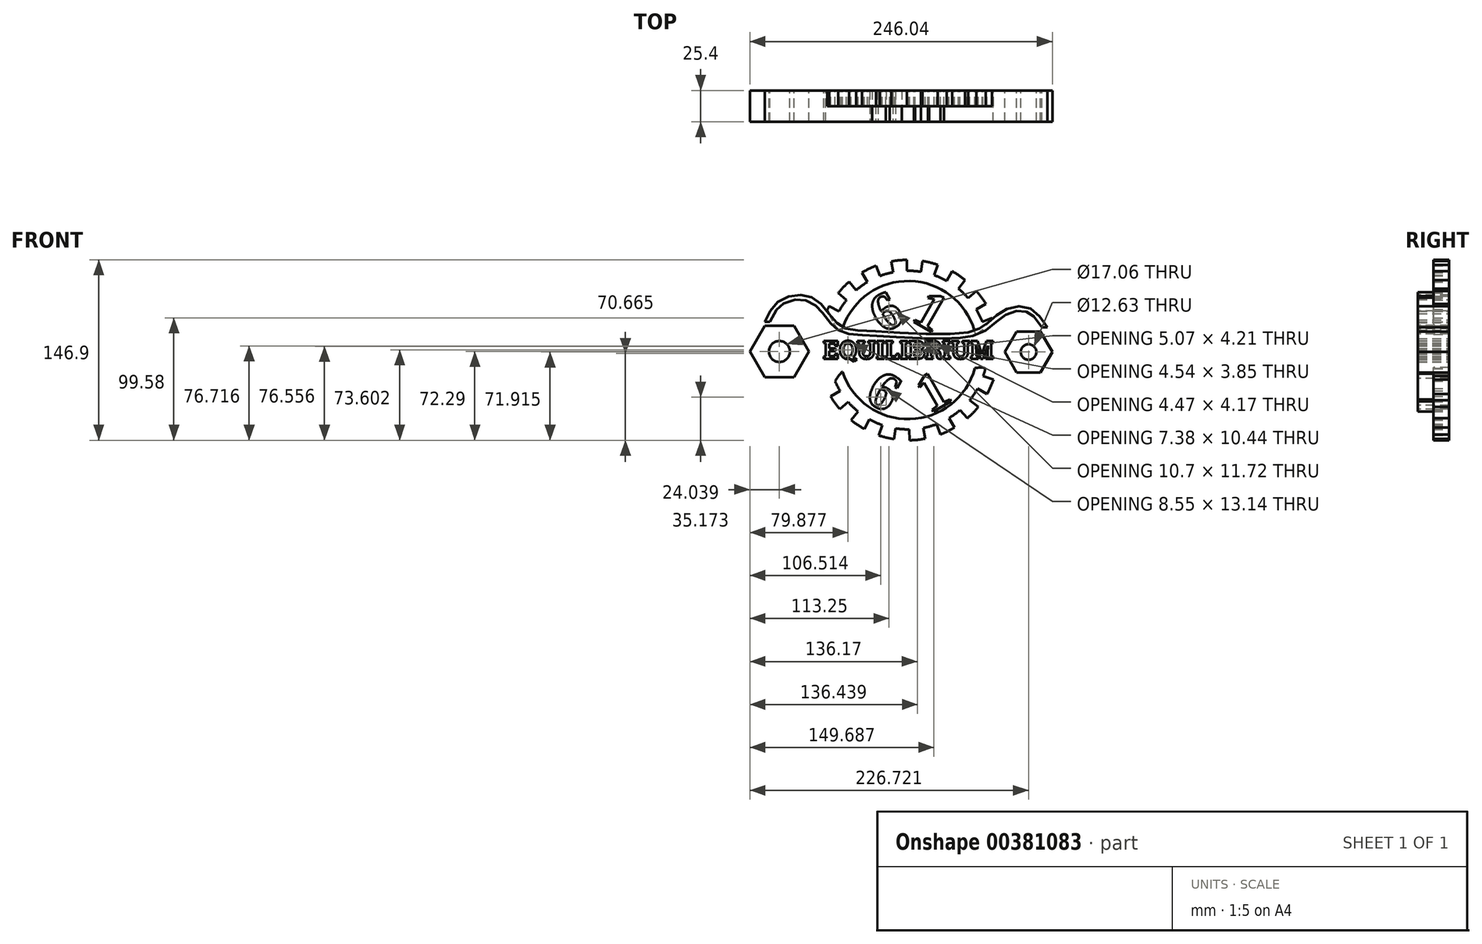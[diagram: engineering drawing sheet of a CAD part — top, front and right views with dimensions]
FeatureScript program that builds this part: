
annotation { "Feature Type Name" : "Feature", "Feature Type Description" : "" }
export const myFeature = defineFeature(function(context is Context, id is Id, definition is map)
    precondition{}
    {
        {
            var Q0;
            Q0=qCreatedBy(makeId("Front.planeOp"),FACE);
            var sketch = newSketch(context, id + "F0", { "sketchPlane" : qUnion([Q0])});
            skCircle(sketch, "E0.cCircle", {"center": v(93.86, 118.06) * mm, "radius": 16.73 * mm, "construction": true});
            skLineSegment(sketch, "E0.0", {"start": v(74.54, 118.06) * mm, "end": v(84.2, 134.79) * mm});
            skLineSegment(sketch, "E0.1", {"start": v(84.2, 134.79) * mm, "end": v(103.52, 134.79) * mm});
            skLineSegment(sketch, "E0.2", {"start": v(103.52, 134.79) * mm, "end": v(113.18, 118.06) * mm});
            skLineSegment(sketch, "E0.3", {"start": v(113.18, 118.06) * mm, "end": v(103.52, 101.32) * mm});
            skLineSegment(sketch, "E0.4", {"start": v(103.52, 101.32) * mm, "end": v(84.2, 101.32) * mm});
            skLineSegment(sketch, "E0.5", {"start": v(84.2, 101.32) * mm, "end": v(74.54, 118.06) * mm});
            skPoint(sketch, "E0.0.midPoint", {"position": v(79.37, 126.42) * mm});
            skCircle(sketch, "E1.cCircle", {"center": v(-108.82, 118.43) * mm, "radius": 20.82 * mm, "construction": true});
            skLineSegment(sketch, "E1.0", {"start": v(-84.78, 118.43) * mm, "end": v(-96.8, 97.61) * mm});
            skLineSegment(sketch, "E1.1", {"start": v(-96.8, 97.61) * mm, "end": v(-120.84, 97.61) * mm});
            skLineSegment(sketch, "E1.2", {"start": v(-120.84, 97.61) * mm, "end": v(-132.86, 118.43) * mm});
            skLineSegment(sketch, "E1.3", {"start": v(-132.86, 118.43) * mm, "end": v(-120.84, 139.25) * mm});
            skLineSegment(sketch, "E1.4", {"start": v(-120.84, 139.25) * mm, "end": v(-96.8, 139.25) * mm});
            skLineSegment(sketch, "E1.5", {"start": v(-96.8, 139.25) * mm, "end": v(-84.78, 118.43) * mm});
            skPoint(sketch, "E1.0.midPoint", {"position": v(-90.8, 108.02) * mm});
            skCircle(sketch, "E2", {"center": v(-108.82, 118.43) * mm, "radius": 8.53 * mm});
            skCircle(sketch, "E3", {"center": v(93.86, 118.06) * mm, "radius": 6.32 * mm});
            skLineSegment(sketch, "E4.0", {"start": v(82.3, 138.1) * mm, "end": v(109.3, 138.1) * mm});
            skLineSegment(sketch, "E4.1", {"start": v(70.73, 118.06) * mm, "end": v(82.3, 138.1) * mm});
            skLineSegment(sketch, "E4.2", {"start": v(82.3, 98.02) * mm, "end": v(70.73, 118.06) * mm});
            skLineSegment(sketch, "E4.3", {"start": v(103.52, 98.02) * mm, "end": v(82.3, 98.02) * mm});
            skLineSegment(sketch, "E5.0", {"start": v(-94.9, 94.3) * mm, "end": v(-120.84, 94.3) * mm});
            skLineSegment(sketch, "E5.1", {"start": v(-80.97, 118.43) * mm, "end": v(-94.9, 94.3) * mm});
            skLineSegment(sketch, "E5.2", {"start": v(-94.9, 142.55) * mm, "end": v(-80.97, 118.43) * mm});
            skLineSegment(sketch, "E5.3", {"start": v(-120.84, 142.55) * mm, "end": v(-94.9, 142.55) * mm});
            skFitSpline(sketch, "E6", {"points": [v(-120.84, 142.55) * mm, v(-109.54, 159.3) * mm, v(-89.24, 164.37) * mm, v(-74.01, 156.03) * mm, v(-59.88, 139.72) * mm, v(-39.18, 135.4) * mm, v(39.48, 133.4) * mm, v(59.02, 140.4) * mm, v(73.53, 151.68) * mm, v(93.84, 154.22) * mm, v(109.43, 137.9) * mm], "startDerivative": vector(96.51, 208.9) * mm, "endDerivative": vector(140.04, -213.02) * mm});
            skFitSpline(sketch, "E7", {"points": [v(-120.84, 94.3) * mm, v(-105.3, 79.6) * mm, v(-87.85, 76.94) * mm, v(-69.52, 87.59) * mm, v(-57.71, 99.33) * mm, v(-35.67, 104.84) * mm, v(44.99, 104.34) * mm, v(59.43, 101.49) * mm, v(73.33, 88.48) * mm, v(88.11, 84.93) * mm, v(100.24, 90.84) * mm, v(103.52, 98.02) * mm], "startDerivative": vector(157.46, -185.5) * mm, "endDerivative": vector(35.32, 133.18) * mm});
            skLineSegment(sketch, "E8.2", {"start": v(-91.96, 145.1) * mm, "end": v(-77.3, 119.7) * mm});
            skLineSegment(sketch, "E8.3", {"start": v(-77.3, 117.16) * mm, "end": v(-91.96, 91.77) * mm});
            skLineSegment(sketch, "E8.4", {"start": v(-94.16, 90.5) * mm, "end": v(-106.94, 90.5) * mm});
            skLineSegment(sketch, "E9.0", {"start": v(81.56, 141.9) * mm, "end": v(96.75, 141.9) * mm});
            skLineSegment(sketch, "E9.1", {"start": v(67.06, 119.33) * mm, "end": v(79.36, 140.63) * mm});
            skLineSegment(sketch, "E9.2", {"start": v(79.36, 95.48) * mm, "end": v(67.06, 116.79) * mm});
            skFitSpline(sketch, "E10.trimOffspring", {"points": [v(-117.38, 140.95) * mm, v(-116.38, 143.13) * mm, v(-114.9, 146.3) * mm, v(-112.76, 150.07) * mm, v(-111.3, 152.18) * mm, v(-110.04, 153.7) * mm, v(-109.04, 154.74) * mm, v(-107.98, 155.7) * mm, v(-106.85, 156.56) * mm, v(-105.6, 157.36) * mm, v(-103.8, 158.33) * mm, v(-101.36, 159.35) * mm, v(-98.2, 160.21) * mm, v(-94.98, 160.7) * mm, v(-92.36, 160.8) * mm, v(-90.37, 160.68) * mm, v(-88.96, 160.5) * mm, v(-87.6, 160.22) * mm, v(-85.89, 159.75) * mm, v(-83.86, 158.93) * mm, v(-81.54, 157.6) * mm, v(-79.66, 156.17) * mm, v(-78.17, 154.83) * mm, v(-77.07, 153.73) * mm, v(-75.96, 152.52) * mm, v(-74.84, 151.2) * mm, v(-73.71, 149.82) * mm, v(-72.2, 147.88) * mm, v(-70.27, 145.36) * mm, v(-67.9, 142.34) * mm, v(-65.8, 139.95) * mm, v(-64, 138.2) * mm, v(-62.83, 137.17) * mm, v(-61.83, 136.42) * mm, v(-60.82, 135.71) * mm, v(-59.51, 134.94) * mm, v(-57.88, 134.17) * mm, v(-55.63, 133.34) * mm, v(-52.7, 132.64) * mm, v(-48.93, 132.16) * mm, v(-45.44, 131.92) * mm, v(-42.35, 131.75) * mm, v(-39.86, 131.62) * mm, v(-37.16, 131.47) * mm, v(-33.3, 131.25) * mm, v(-28, 130.93) * mm, v(-21.08, 130.52) * mm, v(-13.73, 130.1) * mm, v(-3.57, 129.58) * mm, v(6.83, 129.15) * mm, v(16.86, 128.92) * mm, v(24.05, 128.88) * mm, v(30.77, 129) * mm, v(35.86, 129.25) * mm, v(39.58, 129.56) * mm, v(42.16, 129.85) * mm, v(44.55, 130.21) * mm, v(47.52, 130.78) * mm, v(50.84, 131.65) * mm, v(54.34, 133) * mm, v(57.44, 134.62) * mm, v(60.2, 136.47) * mm, v(62.77, 138.52) * mm, v(65.22, 140.66) * mm, v(67.64, 142.8) * mm, v(70.09, 144.84) * mm, v(72.2, 146.41) * mm, v(73.96, 147.55) * mm, v(75.32, 148.33) * mm, v(76.75, 149.05) * mm, v(78.73, 149.91) * mm, v(81.32, 150.78) * mm, v(84.47, 151.43) * mm, v(87.01, 151.6) * mm, v(88.94, 151.5) * mm, v(90.31, 151.3) * mm, v(91.4, 151.03) * mm, v(92.21, 150.76) * mm, v(93, 150.45) * mm, v(93.98, 149.97) * mm, v(95.13, 149.25) * mm, v(96.28, 148.4) * mm, v(97.8, 147.05) * mm, v(99.68, 145.06) * mm, v(101.9, 142.24) * mm, v(104.07, 139.12) * mm, v(105.51, 136.92) * mm, v(106.24, 135.81) * mm]});
            skLineSegment(sketch, "E11.trimOffspring", {"start": v(-110.44, 146.36) * mm, "end": v(-94.16, 146.36) * mm});
            skLineSegment(sketch, "E12.trimOffspring", {"start": v(90.91, 94.21) * mm, "end": v(81.56, 94.21) * mm});
            skFitSpline(sketch, "E13.0", {"points": [v(-118.32, 96.45) * mm, v(-116.68, 94.52) * mm, v(-114.27, 91.67) * mm, v(-111.02, 88.26) * mm, v(-108.57, 85.95) * mm, v(-106.49, 84.29) * mm, v(-104.8, 83.14) * mm, v(-103.52, 82.37) * mm, v(-102.22, 81.7) * mm, v(-100.44, 80.93) * mm, v(-97.24, 79.9) * mm, v(-93.44, 79.5) * mm, v(-90.04, 79.85) * mm, v(-88.1, 80.26) * mm, v(-86.12, 80.82) * mm, v(-83.62, 81.79) * mm, v(-80.63, 83.32) * mm, v(-77.72, 85.15) * mm, v(-74.94, 87.2) * mm, v(-72.78, 89.05) * mm, v(-71.17, 90.56) * mm, v(-69.63, 92.11) * mm, v(-67.77, 94.1) * mm, v(-65.6, 96.5) * mm, v(-63.37, 98.83) * mm, v(-61.38, 100.67) * mm, v(-59.64, 102.03) * mm, v(-57.8, 103.28) * mm, v(-55.34, 104.61) * mm, v(-52.03, 105.85) * mm, v(-48.33, 106.78) * mm, v(-44.13, 107.45) * mm, v(-40.1, 107.85) * mm, v(-36.5, 108.1) * mm, v(-33.59, 108.26) * mm, v(-30.47, 108.38) * mm, v(-26.08, 108.52) * mm, v(-20.2, 108.62) * mm, v(-12.66, 108.67) * mm, v(-4.8, 108.64) * mm, v(5.84, 108.53) * mm, v(19.09, 108.3) * mm, v(31.11, 108) * mm, v(39.32, 107.78) * mm, v(43.72, 107.67) * mm, v(46.7, 107.6) * mm, v(49.4, 107.52) * mm, v(51.75, 107.4) * mm, v(53.9, 107.16) * mm, v(55.46, 106.87) * mm, v(56.97, 106.46) * mm, v(58.43, 105.9) * mm, v(59.85, 105.18) * mm, v(60.98, 104.45) * mm, v(61.86, 103.8) * mm, v(62.72, 103.1) * mm, v(63.77, 102.17) * mm, v(65.01, 100.98) * mm, v(66.65, 99.31) * mm, v(68.7, 97.15) * mm, v(70.75, 95.03) * mm, v(72.4, 93.47) * mm, v(73.62, 92.4) * mm, v(74.83, 91.44) * mm, v(76.01, 90.63) * mm, v(77.22, 89.93) * mm, v(78.83, 89.15) * mm, v(80.87, 88.45) * mm, v(83.35, 88) * mm, v(85.88, 87.95) * mm, v(88.46, 88.28) * mm, v(91.07, 88.97) * mm, v(93.53, 89.97) * mm, v(95.33, 91) * mm, v(96.54, 91.87) * mm, v(97.18, 92.43) * mm, v(97.62, 92.86) * mm, v(98, 93.29) * mm, v(98.58, 94.04) * mm, v(99.2, 95.2) * mm, v(99.8, 96.87) * mm, v(100.15, 98.17) * mm, v(100.33, 98.87) * mm]});
            skPoint(sketch, "E14.visualSharp", {"position": v(-76.57, 118.43) * mm});
            skArc(sketch, "E14.filletArc", {"start": v(-77.3, 117.16) * mm, "mid": v(-76.96, 118.43) * mm, "end": v(-77.3, 119.7) * mm});
            skPoint(sketch, "E15.visualSharp", {"position": v(-92.7, 146.36) * mm});
            skArc(sketch, "E15.filletArc", {"start": v(-91.96, 145.1) * mm, "mid": v(-92.9, 146.02) * mm, "end": v(-94.16, 146.36) * mm});
            skPoint(sketch, "E16.visualSharp", {"position": v(-114.8, 146.36) * mm});
            skArc(sketch, "E16.filletArc", {"start": v(-112.58, 150.27) * mm, "mid": v(-112.67, 147.68) * mm, "end": v(-110.44, 146.36) * mm});
            skPoint(sketch, "E17.visualSharp", {"position": v(-92.7, 90.5) * mm});
            skArc(sketch, "E17.filletArc", {"start": v(-94.16, 90.5) * mm, "mid": v(-92.9, 90.84) * mm, "end": v(-91.96, 91.77) * mm});
            skArc(sketch, "E18.filletArc", {"start": v(-106.94, 90.5) * mm, "mid": v(-109.32, 88.85) * mm, "end": v(-108.61, 86.05) * mm});
            skPoint(sketch, "E19.visualSharp", {"position": v(80.1, 94.21) * mm});
            skArc(sketch, "E19.filletArc", {"start": v(79.36, 95.48) * mm, "mid": v(80.3, 94.55) * mm, "end": v(81.56, 94.21) * mm});
            skPoint(sketch, "E20.visualSharp", {"position": v(66.33, 118.06) * mm});
            skArc(sketch, "E20.filletArc", {"start": v(67.06, 119.33) * mm, "mid": v(66.72, 118.06) * mm, "end": v(67.06, 116.79) * mm});
            skPoint(sketch, "E21.visualSharp", {"position": v(80.1, 141.9) * mm});
            skArc(sketch, "E21.filletArc", {"start": v(81.56, 141.9) * mm, "mid": v(80.3, 141.56) * mm, "end": v(79.36, 140.63) * mm});
            skArc(sketch, "E22.filletArc", {"start": v(91.81, 89.3) * mm, "mid": v(93.41, 92.13) * mm, "end": v(90.91, 94.21) * mm});
            skPoint(sketch, "E23.visualSharp", {"position": v(102.1, 141.9) * mm});
            skArc(sketch, "E23.filletArc", {"start": v(96.75, 141.9) * mm, "mid": v(99.09, 143.43) * mm, "end": v(98.6, 146.18) * mm});
            skSolve(sketch);
        }
        {
            var Q0;
            Q0=qCreatedBy(makeId("Front.planeOp"),FACE);
            var sketch = newSketch(context, id + "F1", { "sketchPlane" : qUnion([Q0])});
            skText(sketch, "E24", { "text": "EQUILIBRIUM", "fontName": "RobotoSlab-Bold.ttf"});
            const initialGuessF1  = {"E24": [-0.07336, 0.11246, 1, 0, 0.01476]};
            skSetInitialGuess(sketch, initialGuessF1);
            skSolve(sketch);
        }
        {
            var Q0;
            Q0=qCreatedBy(makeId("Front.planeOp"),FACE);
            var sketch = newSketch(context, id + "F2", { "sketchPlane" : qUnion([Q0])});
            skArc(sketch, "E25", {"start": v(58.97, 157.29) * mm, "mid": v(55.45, 162.64) * mm, "end": v(51.47, 167.66) * mm});
            skLineSegment(sketch, "E26", {"start": v(-4.07, 119.59) * mm, "end": v(56.26, 142.6) * mm, "construction": true});
            skLineSegment(sketch, "E27", {"start": v(-4.07, 119.59) * mm, "end": v(-69.97, 152.06) * mm, "construction": true});
            skLineSegment(sketch, "E28", {"start": v(-4.07, 119.59) * mm, "end": v(51.34, 152.73) * mm, "construction": true});
            skLineSegment(sketch, "E29", {"start": v(-4.07, 119.59) * mm, "end": v(44.75, 161.85) * mm, "construction": true});
            skLineSegment(sketch, "E30", {"start": v(44.75, 161.85) * mm, "end": v(51.47, 167.66) * mm});
            skLineSegment(sketch, "E31", {"start": v(51.34, 152.73) * mm, "end": v(58.97, 157.29) * mm});
            skLineSegment(sketch, "E32", {"start": v(56.26, 142.6) * mm, "end": v(64.56, 145.77) * mm});
            skArc(sketch, "E33", {"start": v(56.26, 142.6) * mm, "mid": v(54.02, 147.77) * mm, "end": v(51.34, 152.73) * mm});
            skArc(sketch, "E34.1.0", {"start": v(44.75, 161.85) * mm, "mid": v(40.88, 165.94) * mm, "end": v(36.67, 169.68) * mm});
            skLineSegment(sketch, "E34.1.1", {"start": v(36.67, 169.68) * mm, "end": v(42.28, 176.58) * mm});
            skArc(sketch, "E34.1.2", {"start": v(42.28, 176.58) * mm, "mid": v(37.13, 180.4) * mm, "end": v(31.68, 183.76) * mm});
            skLineSegment(sketch, "E34.1.3", {"start": v(27.35, 176) * mm, "end": v(31.68, 183.76) * mm});
            skArc(sketch, "E34.2.0", {"start": v(27.35, 176) * mm, "mid": v(22.31, 178.52) * mm, "end": v(17.08, 180.6) * mm});
            skLineSegment(sketch, "E34.2.1", {"start": v(17.08, 180.6) * mm, "end": v(20, 189) * mm});
            skArc(sketch, "E34.2.2", {"start": v(20, 189) * mm, "mid": v(13.85, 190.83) * mm, "end": v(7.57, 192.12) * mm});
            skLineSegment(sketch, "E34.2.3", {"start": v(6.16, 183.34) * mm, "end": v(7.57, 192.12) * mm});
            skLineSegment(sketch, "E34.2.4", {"start": v(27.35, 176) * mm, "end": v(31.68, 183.76) * mm});
            skArc(sketch, "E34.3.0", {"start": v(6.16, 183.34) * mm, "mid": v(0.57, 184) * mm, "end": v(-5.06, 184.15) * mm});
            skLineSegment(sketch, "E34.3.1", {"start": v(-5.06, 184.15) * mm, "end": v(-5.2, 193.04) * mm});
            skArc(sketch, "E34.3.2", {"start": v(-5.2, 193.04) * mm, "mid": v(-11.6, 192.66) * mm, "end": v(-17.94, 191.73) * mm});
            skLineSegment(sketch, "E34.3.3", {"start": v(-16.26, 183) * mm, "end": v(-17.94, 191.73) * mm});
            skLineSegment(sketch, "E34.3.4", {"start": v(6.16, 183.34) * mm, "end": v(7.57, 192.12) * mm});
            skArc(sketch, "E34.4.0", {"start": v(-16.26, 183) * mm, "mid": v(-21.74, 181.7) * mm, "end": v(-27.09, 179.92) * mm});
            skLineSegment(sketch, "E34.4.1", {"start": v(-27.09, 179.92) * mm, "end": v(-30.25, 188.23) * mm});
            skArc(sketch, "E34.4.2", {"start": v(-30.25, 188.23) * mm, "mid": v(-36.14, 185.68) * mm, "end": v(-41.78, 182.64) * mm});
            skLineSegment(sketch, "E34.4.3", {"start": v(-37.21, 175) * mm, "end": v(-41.78, 182.64) * mm});
            skLineSegment(sketch, "E34.4.4", {"start": v(-16.26, 183) * mm, "end": v(-17.94, 191.73) * mm});
            skArc(sketch, "E34.5.0", {"start": v(-37.21, 175) * mm, "mid": v(-41.92, 171.9) * mm, "end": v(-46.33, 168.41) * mm});
            skLineSegment(sketch, "E34.5.1", {"start": v(-46.33, 168.41) * mm, "end": v(-52.15, 175.13) * mm});
            skArc(sketch, "E34.5.2", {"start": v(-52.15, 175.13) * mm, "mid": v(-56.8, 170.73) * mm, "end": v(-61.07, 165.94) * mm});
            skLineSegment(sketch, "E34.5.3", {"start": v(-54.17, 160.33) * mm, "end": v(-61.07, 165.94) * mm});
            skLineSegment(sketch, "E34.5.4", {"start": v(-37.21, 175) * mm, "end": v(-41.78, 182.64) * mm});
            skArc(sketch, "E34.6.0", {"start": v(-54.17, 160.33) * mm, "mid": v(-57.53, 155.8) * mm, "end": v(-60.48, 151.01) * mm});
            skLineSegment(sketch, "E34.6.1", {"start": v(-60.48, 151.01) * mm, "end": v(-68.25, 155.34) * mm});
            skArc(sketch, "E34.6.2", {"start": v(-68.25, 155.34) * mm, "mid": v(-71.12, 149.61) * mm, "end": v(-73.48, 143.65) * mm});
            skLineSegment(sketch, "E34.6.3", {"start": v(-65.08, 140.74) * mm, "end": v(-73.48, 143.65) * mm});
            skLineSegment(sketch, "E34.6.4", {"start": v(-54.17, 160.33) * mm, "end": v(-61.07, 165.94) * mm});
            skArc(sketch, "E34.7.0", {"start": v(-65.08, 140.74) * mm, "mid": v(-66.7, 135.34) * mm, "end": v(-67.83, 129.82) * mm});
            skLineSegment(sketch, "E34.7.1", {"start": v(-67.83, 129.82) * mm, "end": v(-76.6, 131.23) * mm});
            skArc(sketch, "E34.7.2", {"start": v(-76.6, 131.23) * mm, "mid": v(-77.35, 124.87) * mm, "end": v(-77.53, 118.46) * mm});
            skLineSegment(sketch, "E34.7.3", {"start": v(-68.64, 118.6) * mm, "end": v(-77.53, 118.46) * mm});
            skLineSegment(sketch, "E34.7.4", {"start": v(-65.08, 140.74) * mm, "end": v(-73.48, 143.65) * mm});
            skArc(sketch, "E34.8.0", {"start": v(-68.64, 118.6) * mm, "mid": v(-68.3, 112.98) * mm, "end": v(-67.49, 107.4) * mm});
            skLineSegment(sketch, "E34.8.1", {"start": v(-67.49, 107.4) * mm, "end": v(-76.22, 105.72) * mm});
            skArc(sketch, "E34.8.2", {"start": v(-76.22, 105.72) * mm, "mid": v(-74.73, 99.49) * mm, "end": v(-72.71, 93.4) * mm});
            skLineSegment(sketch, "E34.8.3", {"start": v(-64.4, 96.58) * mm, "end": v(-72.71, 93.4) * mm});
            skLineSegment(sketch, "E34.8.4", {"start": v(-68.64, 118.6) * mm, "end": v(-77.53, 118.46) * mm});
            skArc(sketch, "E34.9.0", {"start": v(-64.4, 96.58) * mm, "mid": v(-62.17, 91.4) * mm, "end": v(-59.5, 86.45) * mm});
            skLineSegment(sketch, "E34.9.1", {"start": v(-59.5, 86.45) * mm, "end": v(-67.12, 81.89) * mm});
            skArc(sketch, "E34.9.2", {"start": v(-67.12, 81.89) * mm, "mid": v(-63.6, 76.54) * mm, "end": v(-59.62, 71.51) * mm});
            skLineSegment(sketch, "E34.9.3", {"start": v(-52.9, 77.33) * mm, "end": v(-59.62, 71.51) * mm});
            skLineSegment(sketch, "E34.9.4", {"start": v(-64.4, 96.58) * mm, "end": v(-72.71, 93.4) * mm});
            skArc(sketch, "E34.10.0", {"start": v(-52.9, 77.33) * mm, "mid": v(-49.03, 73.23) * mm, "end": v(-44.82, 69.5) * mm});
            skLineSegment(sketch, "E34.10.1", {"start": v(-44.82, 69.5) * mm, "end": v(-50.43, 62.6) * mm});
            skArc(sketch, "E34.10.2", {"start": v(-50.43, 62.6) * mm, "mid": v(-45.28, 58.77) * mm, "end": v(-39.83, 55.41) * mm});
            skLineSegment(sketch, "E34.10.3", {"start": v(-35.5, 63.18) * mm, "end": v(-39.83, 55.41) * mm});
            skLineSegment(sketch, "E34.10.4", {"start": v(-52.9, 77.33) * mm, "end": v(-59.62, 71.51) * mm});
            skArc(sketch, "E34.11.0", {"start": v(-35.5, 63.18) * mm, "mid": v(-30.46, 60.66) * mm, "end": v(-25.23, 58.58) * mm});
            skLineSegment(sketch, "E34.11.1", {"start": v(-25.23, 58.58) * mm, "end": v(-28.14, 50.18) * mm});
            skArc(sketch, "E34.11.2", {"start": v(-28.14, 50.18) * mm, "mid": v(-22, 48.35) * mm, "end": v(-15.72, 47.06) * mm});
            skLineSegment(sketch, "E34.11.3", {"start": v(-14.31, 55.83) * mm, "end": v(-15.72, 47.06) * mm});
            skLineSegment(sketch, "E34.11.4", {"start": v(-35.5, 63.18) * mm, "end": v(-39.83, 55.41) * mm});
            skArc(sketch, "E34.12.0", {"start": v(-14.31, 55.83) * mm, "mid": v(-8.72, 55.18) * mm, "end": v(-3.09, 55.02) * mm});
            skLineSegment(sketch, "E34.12.1", {"start": v(-3.09, 55.02) * mm, "end": v(-2.95, 46.14) * mm});
            skArc(sketch, "E34.12.2", {"start": v(-2.95, 46.14) * mm, "mid": v(3.45, 46.51) * mm, "end": v(9.79, 47.45) * mm});
            skLineSegment(sketch, "E34.12.3", {"start": v(8.11, 56.18) * mm, "end": v(9.79, 47.45) * mm});
            skLineSegment(sketch, "E34.12.4", {"start": v(-14.31, 55.83) * mm, "end": v(-15.72, 47.06) * mm});
            skArc(sketch, "E34.13.0", {"start": v(8.11, 56.18) * mm, "mid": v(13.6, 57.48) * mm, "end": v(18.94, 59.26) * mm});
            skLineSegment(sketch, "E34.13.1", {"start": v(18.94, 59.26) * mm, "end": v(22.1, 50.95) * mm});
            skArc(sketch, "E34.13.2", {"start": v(22.1, 50.95) * mm, "mid": v(27.99, 53.5) * mm, "end": v(33.63, 56.54) * mm});
            skLineSegment(sketch, "E34.13.3", {"start": v(29.06, 64.17) * mm, "end": v(33.63, 56.54) * mm});
            skLineSegment(sketch, "E34.13.4", {"start": v(8.11, 56.18) * mm, "end": v(9.79, 47.45) * mm});
            skArc(sketch, "E34.14.0", {"start": v(29.06, 64.17) * mm, "mid": v(33.77, 67.27) * mm, "end": v(38.18, 70.77) * mm});
            skLineSegment(sketch, "E34.14.1", {"start": v(38.18, 70.77) * mm, "end": v(44, 64.04) * mm});
            skArc(sketch, "E34.14.2", {"start": v(44, 64.04) * mm, "mid": v(48.66, 68.44) * mm, "end": v(52.92, 73.24) * mm});
            skLineSegment(sketch, "E34.14.3", {"start": v(46.02, 78.84) * mm, "end": v(52.92, 73.24) * mm});
            skLineSegment(sketch, "E34.14.4", {"start": v(29.06, 64.17) * mm, "end": v(33.63, 56.54) * mm});
            skArc(sketch, "E34.15.0", {"start": v(46.02, 78.84) * mm, "mid": v(49.38, 83.37) * mm, "end": v(52.33, 88.16) * mm});
            skLineSegment(sketch, "E34.15.1", {"start": v(52.33, 88.16) * mm, "end": v(60.1, 83.84) * mm});
            skArc(sketch, "E34.15.2", {"start": v(60.1, 83.84) * mm, "mid": v(62.97, 89.57) * mm, "end": v(65.33, 95.52) * mm});
            skLineSegment(sketch, "E34.15.3", {"start": v(56.93, 98.44) * mm, "end": v(65.33, 95.52) * mm});
            skLineSegment(sketch, "E34.15.4", {"start": v(46.02, 78.84) * mm, "end": v(52.92, 73.24) * mm});
            skArc(sketch, "E34.16.0", {"start": v(56.93, 98.44) * mm, "mid": v(58.54, 103.83) * mm, "end": v(59.68, 109.35) * mm});
            skLineSegment(sketch, "E34.16.1", {"start": v(59.68, 109.35) * mm, "end": v(68.46, 107.94) * mm});
            skArc(sketch, "E34.16.2", {"start": v(68.46, 107.94) * mm, "mid": v(69.2, 114.3) * mm, "end": v(69.38, 120.71) * mm});
            skLineSegment(sketch, "E34.16.3", {"start": v(60.49, 120.58) * mm, "end": v(69.38, 120.71) * mm});
            skLineSegment(sketch, "E34.16.4", {"start": v(56.93, 98.44) * mm, "end": v(65.33, 95.52) * mm});
            skArc(sketch, "E34.17.0", {"start": v(60.49, 120.58) * mm, "mid": v(60.16, 126.2) * mm, "end": v(59.34, 131.77) * mm});
            skLineSegment(sketch, "E34.17.1", {"start": v(59.34, 131.77) * mm, "end": v(68.07, 133.45) * mm});
            skArc(sketch, "E34.17.2", {"start": v(68.07, 133.45) * mm, "mid": v(66.58, 139.69) * mm, "end": v(64.56, 145.77) * mm});
            skLineSegment(sketch, "E34.17.4", {"start": v(60.49, 120.58) * mm, "end": v(69.38, 120.71) * mm});
            skFitSpline(sketch, "E35.0", {"points": [v(-120.84, 142.55) * mm, v(-117.92, 148.88) * mm, v(-112, 161.7) * mm, v(-88.47, 166.8) * mm, v(-73.04, 157.45) * mm, v(-60.47, 136.12) * mm, v(-39.23, 135.81) * mm, v(40.04, 129.9) * mm, v(58.9, 138.9) * mm, v(72.18, 153.46) * mm, v(95.97, 158.33) * mm, v(104.94, 144.72) * mm, v(109.43, 137.9) * mm]});
            skFitSpline(sketch, "E36.0", {"points": [v(-120.84, 94.3) * mm, v(-115.97, 88.57) * mm, v(-106.72, 77.75) * mm, v(-87.25, 74.44) * mm, v(-68.7, 86.7) * mm, v(-57.98, 101.64) * mm, v(-36.08, 106.76) * mm, v(44.95, 104.21) * mm, v(59.5, 104.1) * mm, v(72.26, 86.41) * mm, v(87.82, 83.16) * mm, v(101.34, 89.77) * mm, v(102.86, 95.52) * mm, v(103.52, 98.02) * mm]});
            skCircle(sketch, "E37", {"center": v(-4.07, 119.59) * mm, "radius": 56.23 * mm});
            skSolve(sketch);
        }
        {
            var Q0;
            Q0=qCreatedBy(makeId("Front.planeOp"),FACE);
            var sketch = newSketch(context, id + "F3", { "sketchPlane" : qUnion([Q0])});
            skText(sketch, "E38", { "text": "6", "fontName": "Tinos-Bold.ttf"});
            skPoint(sketch, "E39.0", {"position": v(-3.5, 119.84) * mm});
            skLineSegment(sketch, "E40", {"start": v(-3.5, 119.84) * mm, "end": v(-40.45, 183.81) * mm, "construction": true});
            skLineSegment(sketch, "E41", {"start": v(-3.5, 119.84) * mm, "end": v(33.01, 183.1) * mm, "construction": true});
            skText(sketch, "E42", { "text": "1", "fontName": "Tinos-Bold.ttf"});
            skLineSegment(sketch, "E43", {"start": v(-3.5, 119.84) * mm, "end": v(-3.5, 138.31) * mm, "construction": true});
            skLineSegment(sketch, "E44", {"start": v(-3.5, 119.84) * mm, "end": v(-30.78, 72.6) * mm, "construction": true});
            skLineSegment(sketch, "E45", {"start": v(-3.5, 119.84) * mm, "end": v(24.5, 71.33) * mm, "construction": true});
            skText(sketch, "E46", { "text": "1", "fontName": "Tinos-Bold.ttf"});
            skText(sketch, "E47", { "text": "6", "fontName": "Tinos-Bold.ttf"});
            skCircle(sketch, "E48", {"center": v(-3.5, 119.84) * mm, "radius": 21.76 * mm, "construction": true});
            const initialGuessF3  = {"E38": [-0.02457, 0.1328, 0.86603, 0.5, 0.03175], "E42": [-0.00238, 0.14431, 0.86603, -0.5, 0.03175], "E46": [0.0135, 0.06786, 0.86603, 0.5, 0.03175], "E47": [-0.04045, 0.07937, 0.86603, -0.5, 0.03175]};
            skSetInitialGuess(sketch, initialGuessF3);
            skSolve(sketch);
        }
        {
            var Q0;
            Q0=makeQuery(id+"F2.imprint","IMPRINT",FACE,{"disambiguationData":[TD([[makeQuery(id+"F2.imprint","IMPRINT",EDGE,{"derivedFrom":sQuery(id+"F2.wireOp",EDGE,"E25")}),1.0]])]});
            var Q1;
            {var subQ0=sQuery(id+"F2.wireOp",EDGE,"E34.9.1");Q1=makeQuery(id+"F2.imprint","IMPRINT",FACE,{"disambiguationData":[TD([[makeQuery(id+"F2.imprint","IMPRINT",EDGE,{"derivedFrom":subQ0}),1.0]])]});}
            extrude(context, id + "F4", {"entities" : qUnion([Q0, Q1]), "depth" : 12.7 * mm});
        }
        {
            var Q0;
            {var subQ0=sQuery(id+"F0.wireOp",EDGE,"E4.0");Q0=makeQuery(id+"F0.imprint","IMPRINT",FACE,{"disambiguationData":[TD([[makeQuery(id+"F0.imprint","IMPRINT",EDGE,{"derivedFrom":subQ0}),1.0]])]});}
            var Q1;
            Q1=makeQuery(id+"F0.imprint","IMPRINT",FACE,{"disambiguationData":[TD([[makeQuery(id+"F0.imprint","IMPRINT",EDGE,{"derivedFrom":sQuery(id+"F0.wireOp",EDGE,"E1.0")}),-1.0]])]});
            var Q2;
            Q2=makeQuery(id+"F0.imprint","IMPRINT",FACE,{"disambiguationData":[TD([[makeQuery(id+"F0.imprint","IMPRINT",EDGE,{"derivedFrom":sQuery(id+"F0.wireOp",EDGE,"E0.0")}),-1.0]])]});
            var Q3;
            Q3 = qSketchRegion(id + "F1", true);
            var Q4;
            Q4 = qSketchRegion(id + "F3", true);
            extrude(context, id + "F5", {"entities" : qUnion([Q0, Q1, Q2, Q3, Q4]), "depth" : 25.4 * mm});
        }
    });
